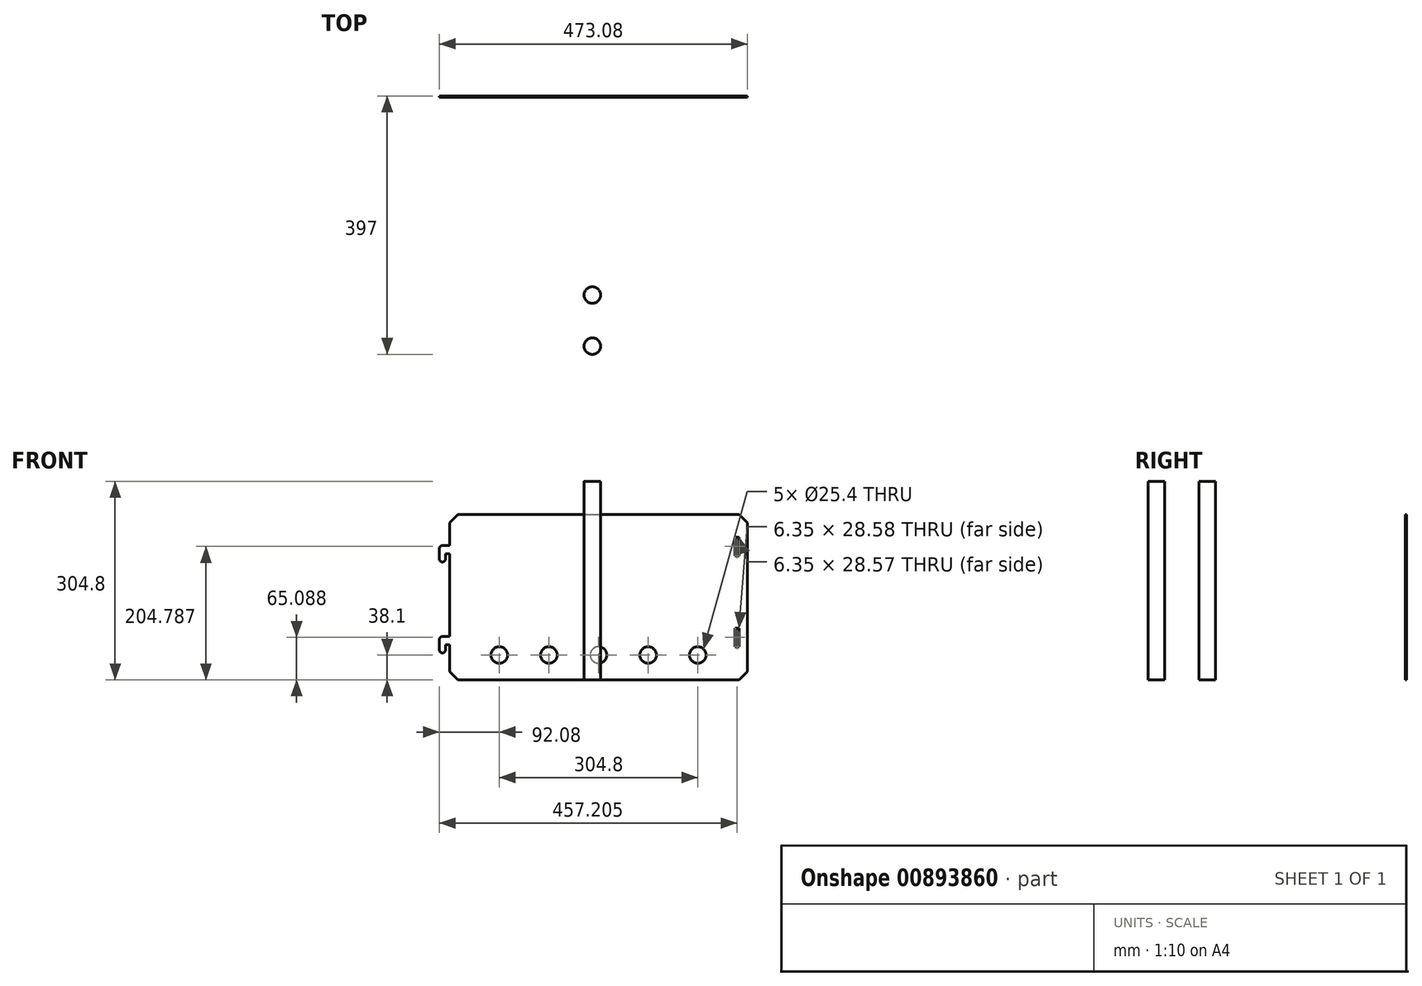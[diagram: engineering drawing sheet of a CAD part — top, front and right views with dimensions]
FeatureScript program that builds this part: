
annotation { "Feature Type Name" : "Feature", "Feature Type Description" : "" }
export const myFeature = defineFeature(function(context is Context, id is Id, definition is map)
    precondition{}
    {
        {
            var Q0;
            Q0=qCreatedBy(makeId("Front.planeOp"),FACE);
            var sketch = newSketch(context, id + "F0", { "sketchPlane" : qUnion([Q0])});
            skLineSegment(sketch, "E0.bottom", {"start": v(0, 0) * mm, "end": v(457.2, 0) * mm});
            skLineSegment(sketch, "E0.top", {"start": v(0, 254) * mm, "end": v(457.2, 254) * mm});
            skLineSegment(sketch, "E0.left", {"start": v(0, 0) * mm, "end": v(0, 254) * mm});
            skLineSegment(sketch, "E0.right", {"start": v(457.2, 0) * mm, "end": v(457.2, 254) * mm});
            skSolve(sketch);
        }
        {
            var Q0;
            Q0 = qSketchRegion(id + "F0", true);
            extrude(context, id + "F1", {"entities" : qUnion([Q0]), "depth" : 2.16 * mm, "offsetDistance" : 25.4 * mm});
        }
        {
            var Q0;
            Q0=makeQuery(id+"F1.opExtrude","CAP_FACE",FACE,{"disambiguationData":[OSD([sQuery(id+"F0.wireOp",EDGE,"E0.bottom"),sQuery(id+"F0.wireOp",EDGE,"E0.top"),sQuery(id+"F0.wireOp",EDGE,"E0.left"),sQuery(id+"F0.wireOp",EDGE,"E0.right")])],"isStart":false});
            var sketch = newSketch(context, id + "F2", { "sketchPlane" : qUnion([Q0])});
            skLineSegment(sketch, "E1", {"start": v(0, 66.67) * mm, "end": v(-15.87, 66.67) * mm});
            skLineSegment(sketch, "E2", {"start": v(-15.88, 66.67) * mm, "end": v(-15.88, 41.27) * mm});
            skLineSegment(sketch, "E3", {"start": v(-15.87, 41.27) * mm, "end": v(-6.35, 41.27) * mm});
            skLineSegment(sketch, "E4", {"start": v(-6.35, 41.28) * mm, "end": v(-6.35, 53.97) * mm});
            skLineSegment(sketch, "E5", {"start": v(-6.35, 53.98) * mm, "end": v(0, 53.98) * mm});
            skLineSegment(sketch, "E6.0.1.0", {"start": v(-15.88, 206.38) * mm, "end": v(-15.88, 180.97) * mm});
            skLineSegment(sketch, "E6.0.1.1", {"start": v(-6.35, 180.98) * mm, "end": v(-6.35, 193.68) * mm});
            skLineSegment(sketch, "E6.0.1.2", {"start": v(-6.35, 193.68) * mm, "end": v(0, 193.68) * mm});
            skLineSegment(sketch, "E6.0.1.3", {"start": v(0, 206.38) * mm, "end": v(-15.88, 206.38) * mm});
            skLineSegment(sketch, "E6.0.1.4", {"start": v(-15.88, 180.98) * mm, "end": v(-6.35, 180.98) * mm});
            skLineSegment(sketch, "E6.direction1", {"start": v(-15.87, 41.27) * mm, "end": v(9.52, 41.27) * mm, "construction": true});
            skLineSegment(sketch, "E6.direction2", {"start": v(-15.87, 41.28) * mm, "end": v(-15.87, 180.97) * mm, "construction": true});
            skSolve(sketch);
        }
        {
            var Q0;
            Q0=makeQuery(id+"F2.imprint","IMPRINT",FACE,{"disambiguationData":[TD([[makeQuery(id+"F2.imprint","IMPRINT",EDGE,{"derivedFrom":sQuery(id+"F2.wireOp",EDGE,"E6.0.1.0")}),1.0]])]});
            var Q1;
            {var subQ0=sQuery(id+"F2.wireOp",EDGE,"E1");Q1=makeQuery(id+"F2.imprint","IMPRINT",FACE,{"disambiguationData":[TD([[makeQuery(id+"F2.imprint","IMPRINT",EDGE,{"derivedFrom":subQ0}),1.0]])]});}
            extrude(context, id + "F3", {"entities" : qUnion([Q0, Q1]), "operationType" : NewBodyOperationType.ADD, "oppositeDirection" : true, "depth" : 2.16 * mm, "offsetDistance" : 25.4 * mm});
        }
        {
            var Q0;
            {var subQ0=sQuery(id+"F0.wireOp",EDGE,"E0.left");Q0=makeQuery(id+"F3.boolean.opBoolean","MERGE",FACE,{"derivedFrom":[makeQuery(id+"F1.opExtrude","CAP_FACE",FACE,{"disambiguationData":[OSD([sQuery(id+"F0.wireOp",EDGE,"E0.bottom"),sQuery(id+"F0.wireOp",EDGE,"E0.top"),subQ0,sQuery(id+"F0.wireOp",EDGE,"E0.right")])],"isStart":false}),makeQuery(id+"F3.opExtrude","CAP_FACE",FACE,{"disambiguationData":[OSD([subQ0,sQuery(id+"F2.wireOp",EDGE,"E1"),sQuery(id+"F2.wireOp",EDGE,"E2"),sQuery(id+"F2.wireOp",EDGE,"E3"),sQuery(id+"F2.wireOp",EDGE,"E4"),sQuery(id+"F2.wireOp",EDGE,"E5")])],"isStart":true}),makeQuery(id+"F3.opExtrude","CAP_FACE",FACE,{"disambiguationData":[OSD([subQ0,sQuery(id+"F2.wireOp",EDGE,"E6.0.1.0"),sQuery(id+"F2.wireOp",EDGE,"E6.0.1.1"),sQuery(id+"F2.wireOp",EDGE,"E6.0.1.2"),sQuery(id+"F2.wireOp",EDGE,"E6.0.1.3"),sQuery(id+"F2.wireOp",EDGE,"E6.0.1.4")])],"isStart":true})]});}
            var sketch = newSketch(context, id + "F4", { "sketchPlane" : qUnion([Q0])});
            skLineSegment(sketch, "E7.bottom", {"start": v(438.15, 219.08) * mm, "end": v(444.5, 219.08) * mm});
            skLineSegment(sketch, "E7.top", {"start": v(438.15, 190.5) * mm, "end": v(444.5, 190.5) * mm});
            skLineSegment(sketch, "E7.left", {"start": v(438.15, 219.08) * mm, "end": v(438.15, 190.5) * mm});
            skLineSegment(sketch, "E7.right", {"start": v(444.5, 219.08) * mm, "end": v(444.5, 190.5) * mm});
            skLineSegment(sketch, "E8.bottom", {"start": v(438.15, 79.38) * mm, "end": v(444.5, 79.38) * mm});
            skLineSegment(sketch, "E8.top", {"start": v(438.15, 50.8) * mm, "end": v(444.5, 50.8) * mm});
            skLineSegment(sketch, "E8.left", {"start": v(438.15, 79.38) * mm, "end": v(438.15, 50.8) * mm});
            skLineSegment(sketch, "E8.right", {"start": v(444.5, 79.38) * mm, "end": v(444.5, 50.8) * mm});
            skSolve(sketch);
        }
        {
            var Q0;
            Q0 = qSketchRegion(id + "F4", true);
            extrude(context, id + "F5", {"entities" : qUnion([Q0]), "operationType" : NewBodyOperationType.REMOVE, "endBound" : BoundingType.THROUGH_ALL, "oppositeDirection" : true, "depth" : 25.4 * mm, "offsetDistance" : 25.4 * mm});
        }
        {
            var Q0;
            Q0=qCreatedBy(makeId("Top.planeOp"),FACE);
            var sketch = newSketch(context, id + "F6", { "sketchPlane" : qUnion([Q0])});
            skCircle(sketch, "E9.cCircle", {"center": v(219.1, -384.3) * mm, "radius": 382.14 * mm, "construction": true});
            skLineSegment(sketch, "E9.0", {"start": v(439.74, -2.16) * mm, "end": v(660.37, -384.3) * mm});
            skLineSegment(sketch, "E9.1", {"start": v(660.37, -384.3) * mm, "end": v(439.74, -766.45) * mm});
            skLineSegment(sketch, "E9.2", {"start": v(439.74, -766.45) * mm, "end": v(-1.52, -766.45) * mm});
            skLineSegment(sketch, "E9.3", {"start": v(-1.52, -766.45) * mm, "end": v(-222.15, -384.3) * mm});
            skLineSegment(sketch, "E9.4", {"start": v(-222.15, -384.3) * mm, "end": v(-1.52, -2.16) * mm});
            skLineSegment(sketch, "E9.5", {"start": v(-1.52, -2.16) * mm, "end": v(439.74, -2.16) * mm});
            skPoint(sketch, "E9.0.midPoint", {"position": v(550.05, -193.23) * mm});
            skPoint(sketch, "E10", {"position": v(439.74, -2.16) * mm});
            skCircle(sketch, "E11", {"center": v(219.1, -384.3) * mm, "radius": 12.7 * mm});
            skSolve(sketch);
        }
        {
            var Q0;
            Q0=makeQuery(id+"F6.imprint","IMPRINT",FACE,{"disambiguationData":[TD([[makeQuery(id+"F6.imprint","IMPRINT",EDGE,{"derivedFrom":sQuery(id+"F6.wireOp",EDGE,"E11")}),1.0]])]});
            extrude(context, id + "F7", {"entities" : qUnion([Q0]), "depth" : 304.8 * mm, "offsetDistance" : 25.4 * mm});
        }
        {
            var Q0;
            Q0=qCreatedBy(makeId("Top.planeOp"),FACE);
            var sketch = newSketch(context, id + "F8", { "sketchPlane" : qUnion([Q0])});
            skCircle(sketch, "E12.cCircle", {"center": v(219.08, -305.87) * mm, "radius": 303.72 * mm, "construction": true});
            skLineSegment(sketch, "E12.0", {"start": v(439.74, -2.16) * mm, "end": v(576.11, -421.88) * mm});
            skLineSegment(sketch, "E12.1", {"start": v(576.11, -421.88) * mm, "end": v(219.08, -681.29) * mm});
            skLineSegment(sketch, "E12.2", {"start": v(219.07, -681.29) * mm, "end": v(-137.96, -421.88) * mm});
            skLineSegment(sketch, "E12.3", {"start": v(-137.96, -421.88) * mm, "end": v(-1.59, -2.16) * mm});
            skLineSegment(sketch, "E12.4", {"start": v(-1.59, -2.16) * mm, "end": v(439.74, -2.16) * mm});
            skPoint(sketch, "E12.0.midPoint", {"position": v(507.93, -212.02) * mm});
            skCircle(sketch, "E13", {"center": v(219.08, -305.87) * mm, "radius": 12.7 * mm});
            skSolve(sketch);
        }
        {
            var Q0;
            Q0=makeQuery(id+"F8.imprint","IMPRINT",FACE,{"disambiguationData":[TD([[makeQuery(id+"F8.imprint","IMPRINT",EDGE,{"derivedFrom":sQuery(id+"F8.wireOp",EDGE,"E13")}),1.0]])]});
            extrude(context, id + "F9", {"entities" : qUnion([Q0]), "depth" : 304.8 * mm, "offsetDistance" : 25.4 * mm});
        }
        {
            var Q0;
            Q0=makeQuery(id+"F3.opExtrude","SWEPT_EDGE",EDGE,{"disambiguationData":[OSD([sQuery(id+"F2.wireOp",EDGE,"E6.0.1.0"),sQuery(id+"F2.wireOp",EDGE,"E6.0.1.3")])]});
            var Q1;
            Q1=makeQuery(id+"F3.opExtrude","SWEPT_EDGE",EDGE,{"disambiguationData":[OSD([sQuery(id+"F2.wireOp",EDGE,"E1"),sQuery(id+"F2.wireOp",EDGE,"E2")])]});
            var Q2;
            Q2=makeQuery(id+"F3.opExtrude","SWEPT_EDGE",EDGE,{"disambiguationData":[OSD([sQuery(id+"F2.wireOp",EDGE,"E2"),sQuery(id+"F2.wireOp",EDGE,"E3")])]});
            var Q3;
            Q3=makeQuery(id+"F3.opExtrude","SWEPT_EDGE",EDGE,{"disambiguationData":[OSD([sQuery(id+"F2.wireOp",EDGE,"E3"),sQuery(id+"F2.wireOp",EDGE,"E4")])]});
            var Q4;
            Q4=makeQuery(id+"F3.opExtrude","SWEPT_EDGE",EDGE,{"disambiguationData":[OSD([sQuery(id+"F2.wireOp",EDGE,"E6.0.1.0"),sQuery(id+"F2.wireOp",EDGE,"E6.0.1.4")])]});
            var Q5;
            Q5=makeQuery(id+"F3.opExtrude","SWEPT_EDGE",EDGE,{"disambiguationData":[OSD([sQuery(id+"F2.wireOp",EDGE,"E6.0.1.1"),sQuery(id+"F2.wireOp",EDGE,"E6.0.1.4")])]});
            chamfer(context, id + "F10", {"entities" : qUnion([Q0, Q1, Q2, Q3, Q4, Q5]), "width" : 3.17 * mm, "tangentPropagation" : true});
        }
        {
            var Q0;
            Q0=makeQuery(id+"F1.opExtrude","SWEPT_EDGE",EDGE,{"disambiguationData":[OSD([sQuery(id+"F0.wireOp",EDGE,"E0.top"),sQuery(id+"F0.wireOp",EDGE,"E0.left")])]});
            var Q1;
            Q1=makeQuery(id+"F1.opExtrude","SWEPT_EDGE",EDGE,{"disambiguationData":[OSD([sQuery(id+"F0.wireOp",EDGE,"E0.bottom"),sQuery(id+"F0.wireOp",EDGE,"E0.left")])]});
            var Q2;
            Q2=makeQuery(id+"F1.opExtrude","SWEPT_EDGE",EDGE,{"disambiguationData":[OSD([sQuery(id+"F0.wireOp",EDGE,"E0.bottom"),sQuery(id+"F0.wireOp",EDGE,"E0.right")])]});
            var Q3;
            Q3=makeQuery(id+"F1.opExtrude","SWEPT_EDGE",EDGE,{"disambiguationData":[OSD([sQuery(id+"F0.wireOp",EDGE,"E0.top"),sQuery(id+"F0.wireOp",EDGE,"E0.right")])]});
            chamfer(context, id + "F11", {"entities" : qUnion([Q0, Q1, Q2, Q3]), "width" : 12.7 * mm, "tangentPropagation" : true});
        }
        {
            var Q0;
            {var subQ0=sQuery(id+"F0.wireOp",EDGE,"E0.left");Q0=makeQuery(id+"F3.boolean.opBoolean","MERGE",FACE,{"derivedFrom":[makeQuery(id+"F1.opExtrude","CAP_FACE",FACE,{"disambiguationData":[OSD([sQuery(id+"F0.wireOp",EDGE,"E0.bottom"),sQuery(id+"F0.wireOp",EDGE,"E0.top"),subQ0,sQuery(id+"F0.wireOp",EDGE,"E0.right")])],"isStart":false}),makeQuery(id+"F3.opExtrude","CAP_FACE",FACE,{"disambiguationData":[OSD([subQ0,sQuery(id+"F2.wireOp",EDGE,"E1"),sQuery(id+"F2.wireOp",EDGE,"E2"),sQuery(id+"F2.wireOp",EDGE,"E3"),sQuery(id+"F2.wireOp",EDGE,"E4"),sQuery(id+"F2.wireOp",EDGE,"E5")])],"isStart":true}),makeQuery(id+"F3.opExtrude","CAP_FACE",FACE,{"disambiguationData":[OSD([subQ0,sQuery(id+"F2.wireOp",EDGE,"E6.0.1.0"),sQuery(id+"F2.wireOp",EDGE,"E6.0.1.1"),sQuery(id+"F2.wireOp",EDGE,"E6.0.1.2"),sQuery(id+"F2.wireOp",EDGE,"E6.0.1.3"),sQuery(id+"F2.wireOp",EDGE,"E6.0.1.4")])],"isStart":true})]});}
            var sketch = newSketch(context, id + "F12", { "sketchPlane" : qUnion([Q0])});
            skCircle(sketch, "E14", {"center": v(76.2, 38.1) * mm, "radius": 12.7 * mm});
            skCircle(sketch, "E15.1.0.0", {"center": v(152.4, 38.1) * mm, "radius": 12.7 * mm});
            skCircle(sketch, "E15.2.0.0", {"center": v(228.6, 38.1) * mm, "radius": 12.7 * mm});
            skCircle(sketch, "E15.3.0.0", {"center": v(304.8, 38.1) * mm, "radius": 12.7 * mm});
            skCircle(sketch, "E15.4.0.0", {"center": v(381, 38.1) * mm, "radius": 12.7 * mm});
            skLineSegment(sketch, "E15.direction1", {"start": v(76.2, 38.1) * mm, "end": v(152.4, 38.1) * mm, "construction": true});
            skSolve(sketch);
        }
        {
            var Q0;
            Q0 = qSketchRegion(id + "F12", true);
            extrude(context, id + "F13", {"entities" : qUnion([Q0]), "operationType" : NewBodyOperationType.REMOVE, "endBound" : BoundingType.THROUGH_ALL, "oppositeDirection" : true, "depth" : 25.4 * mm, "offsetDistance" : 25.4 * mm});
        }
    });
